# Revit family: Zumtobel CLEAN
name_source: partatom
category: Leuchten
revit_build: Autodesk Revit 2016 (Build: 20150714_1515(x64)
units: mm (PartAtom-declared; Revit-internal decimal feet)

## family parameters
Basisbauteil = Fläche
Beim Laden mit Abzugskörper schneiden = Nein
Bemaßung runder Anschluss = Durchmesser verwenden
Gemeinsam genutzt = Nein
Lichtquelle = Ja
OmniClass-Nummer = 23.80.70.11
OmniClass-Titel = Luminaries for Internal Lighting
Raumberechnungspunkt = Nein
Teiletyp = Normal

## types (9) — shared parameters
Baugruppenkennzeichen = D5020200
Beschreibung = Ceiling recessed luminaire
Body = Zumtobel_Metal_Aluminium
Cover = Zumtobel_PMMA_Self_llumination_Opaque
Emissionsform beim Rendern sichtbar = Nein
Farbfilter = 16777215
Farbtemperaturverschiebung bei Dämpfen der Lampe = <Keine Auswahl>
Hersteller = Zumtobel Lighting
Neigungswinkel = 90.00°
URL = http://www.zumtobel.com
Voltage = 230 V
zero-valued in all types: Vorgabe-Ansicht

## per-type parameters (varying)
| type | Cover 1 | Cover 2 | Datei für fotometrisches Netz | Height | Lampe | Length | Modell | Scheinlast | Von Breite des Rechtecks ausssenden | Von Länge des Rechtecks aussenden | Width |
| CLEAN C-O 2/54W T16 M625 PM | Ja | Nein | D23350V8.IES | 101 mm  [stored 0.331365 ft] | T16 | 1248 mm  [stored 4.09449 ft] | 42159490 | 115 VA | 1203 mm  [stored 3.94685 ft] | 265 mm  [stored 0.869423 ft] | 310 mm  [stored 1.01706 ft] |
| CLEAN A-MP LED6000-840 M600Q | Ja | Nein | 42182678_(STD).IES | 106 mm  [stored 0.347769 ft] | LED | 598 mm  [stored 1.96194 ft] | 42182678 | 55 VA | 553 mm  [stored 1.8143 ft] | 553 mm  [stored 1.8143 ft] | 598 mm  [stored 1.96194 ft] |
| CLEAN A-MP LED4000-840 M600Q | Ja | Nein | 42182682_(STD).IES | 106 mm  [stored 0.347769 ft] | LED | 598 mm  [stored 1.96194 ft] | 42182682
42182682 | 33 VA | 553 mm  [stored 1.8143 ft] | 553 mm  [stored 1.8143 ft] | 598 mm  [stored 1.96194 ft] |
| CLEAN A-MP LED4000-840 M600L | Ja | Nein | 42182681_(STD).IES | 106 mm  [stored 0.347769 ft] | LED | 1184 mm  [stored 3.88451 ft] | 42182681 | 36 VA | 1139 mm  [stored 3.73688 ft] | 232 mm  [stored 0.761155 ft] | 277 mm  [stored 0.908793 ft] |
| CLEAN A-MP LED6200-940 M625Q | Ja | Nein | 42183017_(STD_LEO).IES | 106 mm  [stored 0.347769 ft] | LED | 623 mm  [stored 2.04396 ft] | 42183017 | 71 VA | 578 mm | 578 mm | 623 mm  [stored 2.04396 ft] |
| CLEAN C-O LED4800-940 M600L LDO | Nein | Ja | 42183187_(STD_LEO).IES | 101 mm  [stored 0.331365 ft] | LED | 1198 mm  [stored 3.93045 ft] | 42183187 | 49 VA | 1153 mm  [stored 3.78281 ft] | 253 mm  [stored 0.830052 ft] | 298 mm  [stored 0.97769 ft] |
| CLEAN C-O LED5000-840 M600L LDO | Nein | Ja | 42183179_(STD_LEO).IES | 101 mm  [stored 0.331365 ft] | LED | 1198 mm  [stored 3.93045 ft] | 42183179 | 45 VA | 1153 mm  [stored 3.78281 ft] | 253 mm  [stored 0.830052 ft] | 298 mm  [stored 0.97769 ft] |
| CLEAN A-MP LED4600-940 M600L LDO | Ja | Nein | 42183015_(STD_LEO).IES | 106 mm  [stored 0.347769 ft] | LED | 1198 mm  [stored 3.93045 ft] | 42183015 | 44 VA | 1153 mm  [stored 3.78281 ft] | 253 mm  [stored 0.830052 ft] | 298 mm  [stored 0.97769 ft] |
| CLEAN A-MP LED4800-940 M625L | Ja | Nein | D32475AA_CLEAN_A-MP_LED4800-940_M625L.IES | 106 mm  [stored 0.347769 ft] | LED | 1248 mm  [stored 4.09449 ft] | 42183019 | 44 VA | 1203 mm  [stored 3.94685 ft] | 265 mm  [stored 0.869423 ft] | 310 mm  [stored 1.01706 ft] |

note: [stored X ft] marks values corroborated as IEEE doubles in the binary element streams (Revit-internal decimal feet)

## geometry (parser evidence)
native form markers: Blend x2, Sweep x3
no freeform markers — native parametric forms only
